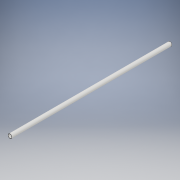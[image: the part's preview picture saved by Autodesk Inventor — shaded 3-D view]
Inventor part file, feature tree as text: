
AUTODESK INVENTOR PART (.ipt)
format: ipt  version: 2019 (Build 230136000, 136)  size: 96,256 bytes
history: native  units: mm
features: extrude x1, sketch x1
ambient origin geometry x8: Origin, YZ Plane, XZ Plane, XY Plane, X Axis, Y Axis, Z Axis, Center Point
bodies: Solide1 (feature_tree)
feature tree (2):
  extrude  "Extrusion1"  Depth=22.0mm
  sketch  "Esquisse1"
